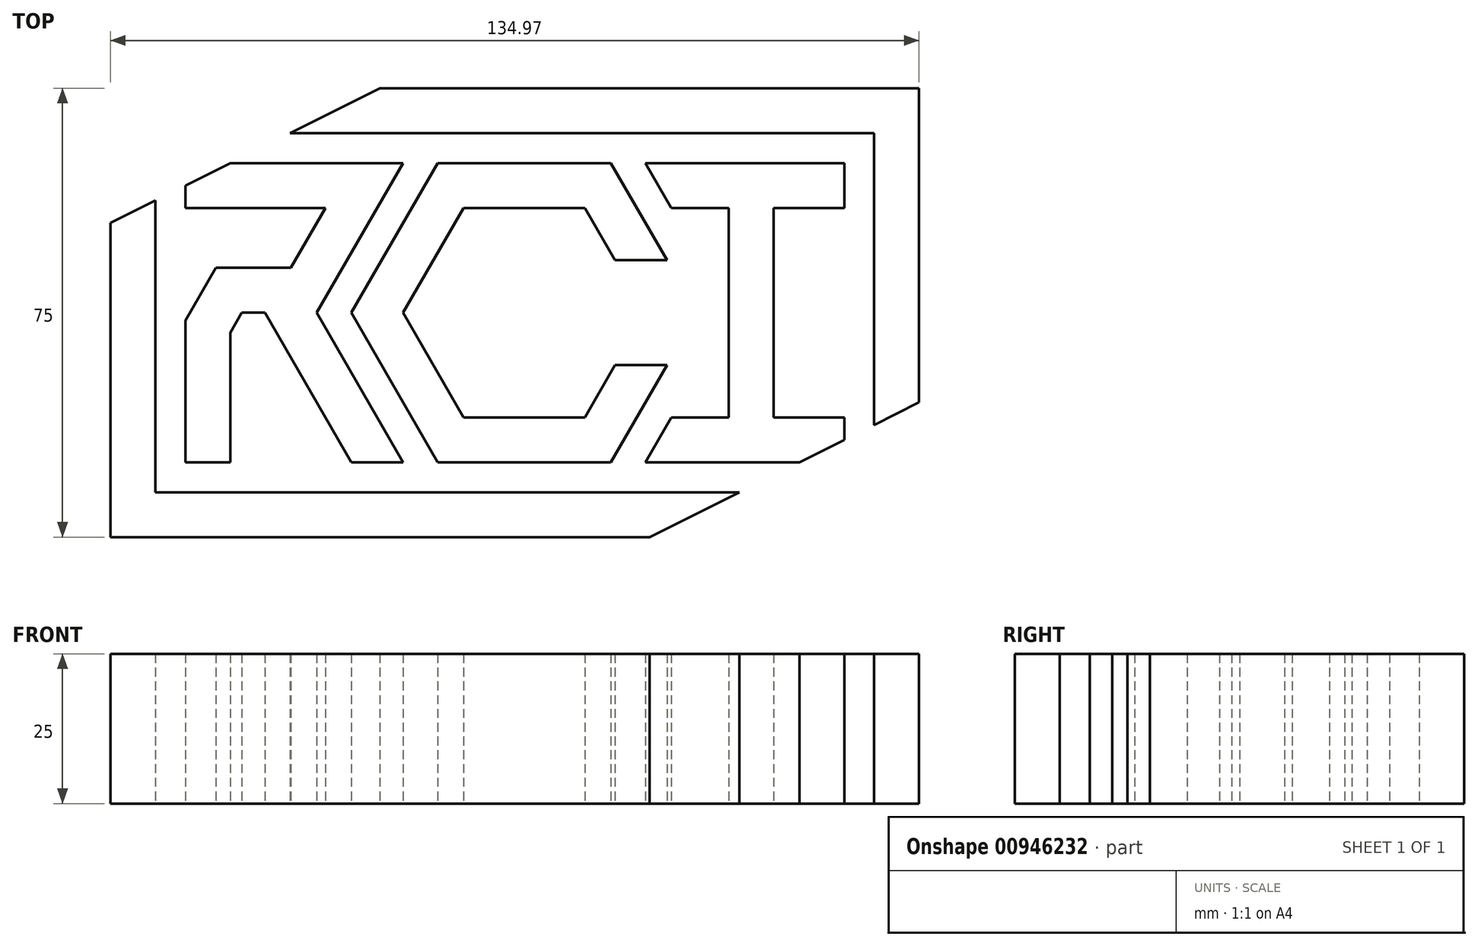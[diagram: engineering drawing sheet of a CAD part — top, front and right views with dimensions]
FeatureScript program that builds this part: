
annotation { "Feature Type Name" : "Feature", "Feature Type Description" : "" }
export const myFeature = defineFeature(function(context is Context, id is Id, definition is map)
    precondition{}
    {
        {
            var Q0;
            Q0=qCreatedBy(makeId("Top.planeOp"),FACE);
            var sketch = newSketch(context, id + "F0", { "sketchPlane" : qUnion([Q0])});
            skCircle(sketch, "E0.cCircle", {"center": v(0, 0) * mm, "radius": 17.5 * mm, "construction": true});
            skLineSegment(sketch, "E0.0", {"start": v(-10.1, 17.5) * mm, "end": v(10.1, 17.5) * mm});
            skLineSegment(sketch, "E0.1", {"start": v(10.1, 17.5) * mm, "end": v(15.16, 8.75) * mm});
            skLineSegment(sketch, "E0.2", {"start": v(15.16, -8.75) * mm, "end": v(10.1, -17.5) * mm});
            skLineSegment(sketch, "E0.3", {"start": v(10.1, -17.5) * mm, "end": v(-10.1, -17.5) * mm});
            skLineSegment(sketch, "E0.4", {"start": v(-10.1, -17.5) * mm, "end": v(-20.2, 0) * mm});
            skLineSegment(sketch, "E0.5", {"start": v(-20.2, 0) * mm, "end": v(-10.1, 17.5) * mm});
            skPoint(sketch, "E0.0.midPoint", {"position": v(0, 17.5) * mm});
            skLineSegment(sketch, "E1.0", {"start": v(-14.43, 25) * mm, "end": v(14.43, 25) * mm});
            skLineSegment(sketch, "E1.1", {"start": v(23.82, -8.75) * mm, "end": v(14.43, -25) * mm});
            skLineSegment(sketch, "E1.2", {"start": v(14.43, -25) * mm, "end": v(-14.43, -25) * mm});
            skLineSegment(sketch, "E1.3", {"start": v(14.43, 25) * mm, "end": v(23.82, 8.75) * mm});
            skLineSegment(sketch, "E1.4", {"start": v(-14.43, -25) * mm, "end": v(-28.87, 0) * mm});
            skLineSegment(sketch, "E1.5", {"start": v(-28.87, 0) * mm, "end": v(-14.43, 25) * mm});
            skPoint(sketch, "E2", {"position": v(15.16, -8.75) * mm});
            skPoint(sketch, "E3", {"position": v(15.16, 8.75) * mm});
            skLineSegment(sketch, "E4", {"start": v(15.16, 8.75) * mm, "end": v(23.82, 8.75) * mm});
            skLineSegment(sketch, "E5", {"start": v(15.16, -8.75) * mm, "end": v(23.82, -8.75) * mm});
            skPoint(sketch, "E6.orphan", {"position": v(20.2, 0) * mm});
            skLineSegment(sketch, "E7", {"start": v(85.6, -25) * mm, "end": v(-85.44, -25) * mm, "construction": true});
            skLineSegment(sketch, "E8", {"start": v(-85.44, -25) * mm, "end": v(-85.44, 25) * mm, "construction": true});
            skLineSegment(sketch, "E9", {"start": v(85.6, 25) * mm, "end": v(85.6, -25) * mm, "construction": true});
            skLineSegment(sketch, "E10", {"start": v(-85.44, 25) * mm, "end": v(0, 25) * mm, "construction": true});
            skPoint(sketch, "E11", {"position": v(0, 25) * mm});
            skLineSegment(sketch, "E12.0", {"start": v(-34.64, 0) * mm, "end": v(-23.24, 19.75) * mm});
            skLineSegment(sketch, "E12.1", {"start": v(-20.2, -25) * mm, "end": v(-34.64, 0) * mm});
            skLineSegment(sketch, "E13.0", {"start": v(-38.97, 7.5) * mm, "end": v(-33.2, 17.5) * mm});
            skLineSegment(sketch, "E13.1", {"start": v(-28.87, -25) * mm, "end": v(-43.3, 0) * mm});
            skLineSegment(sketch, "E14", {"start": v(-20.2, 25) * mm, "end": v(-49.07, 25) * mm});
            skLineSegment(sketch, "E15.0", {"start": v(-33.2, 17.5) * mm, "end": v(-49.07, 17.5) * mm});
            skLineSegment(sketch, "E16", {"start": v(-43.3, 0) * mm, "end": v(-47.15, 0) * mm});
            skLineSegment(sketch, "E17.0", {"start": v(-38.97, 7.5) * mm, "end": v(-49.07, 7.5) * mm});
            skLineSegment(sketch, "E18", {"start": v(-20.2, -25) * mm, "end": v(-28.87, -25) * mm});
            skLineSegment(sketch, "E19", {"start": v(-49.07, -3.33) * mm, "end": v(-49.07, -25) * mm});
            skLineSegment(sketch, "E20.0", {"start": v(-56.57, -1.32) * mm, "end": v(-56.57, -25) * mm});
            skLineSegment(sketch, "E21", {"start": v(-56.57, -25) * mm, "end": v(-49.07, -25) * mm});
            skLineSegment(sketch, "E22", {"start": v(-49.07, 7.5) * mm, "end": v(-51.48, 7.5) * mm});
            skLineSegment(sketch, "E23", {"start": v(-51.48, 7.5) * mm, "end": v(-56.57, -1.32) * mm});
            skLineSegment(sketch, "E24", {"start": v(-49.07, 25) * mm, "end": v(-56.57, 21.25) * mm});
            skLineSegment(sketch, "E25", {"start": v(-56.57, 21.25) * mm, "end": v(-56.57, 17.5) * mm});
            skLineSegment(sketch, "E26", {"start": v(-49.07, 17.5) * mm, "end": v(-56.57, 17.5) * mm});
            skLineSegment(sketch, "E27", {"start": v(-23.24, 19.75) * mm, "end": v(-20.2, 25) * mm});
            skLineSegment(sketch, "E28", {"start": v(-77.06, 17.5) * mm, "end": v(-77.06, 25) * mm, "construction": true});
            skPoint(sketch, "E29", {"position": v(-77.06, 21.25) * mm});
            skLineSegment(sketch, "E30", {"start": v(-77.06, 17.5) * mm, "end": v(-85.44, 17.5) * mm, "construction": true});
            skLineSegment(sketch, "E31", {"start": v(-56.57, -25) * mm, "end": v(-85.44, -25) * mm, "construction": true});
            skLineSegment(sketch, "E32", {"start": v(0, 25) * mm, "end": v(85.6, 25) * mm, "construction": true});
            skLineSegment(sketch, "E33.0", {"start": v(-47.15, 0) * mm, "end": v(-49.07, -3.33) * mm});
            skPoint(sketch, "E34.orphan", {"position": v(-49.07, 0) * mm});
            skLineSegment(sketch, "E35", {"start": v(20.2, 25) * mm, "end": v(53.4, 25) * mm});
            skLineSegment(sketch, "E36", {"start": v(53.4, 25) * mm, "end": v(53.4, 17.5) * mm});
            skLineSegment(sketch, "E37", {"start": v(53.4, 17.5) * mm, "end": v(24.54, 17.5) * mm});
            skLineSegment(sketch, "E38", {"start": v(24.54, 17.5) * mm, "end": v(20.2, 25) * mm});
            skLineSegment(sketch, "E39", {"start": v(0, 0) * mm, "end": v(85.6, 0) * mm, "construction": true});
            skLineSegment(sketch, "E40.MirrorCS", {"start": v(53.4, -17.5) * mm, "end": v(41.64, -17.5) * mm});
            skLineSegment(sketch, "E41.MirrorCS", {"start": v(24.54, -17.5) * mm, "end": v(20.2, -25) * mm});
            skLineSegment(sketch, "E42.MirrorCS", {"start": v(20.2, -25) * mm, "end": v(53.4, -25) * mm});
            skLineSegment(sketch, "E43.MirrorCS", {"start": v(53.4, -21.25) * mm, "end": v(53.4, -17.5) * mm});
            skLineSegment(sketch, "E44", {"start": v(53.4, -21.25) * mm, "end": v(45.9, -25) * mm});
            skPoint(sketch, "E45.orphan", {"position": v(53.4, -25) * mm});
            skPoint(sketch, "E46", {"position": v(38.97, 17.5) * mm});
            skPoint(sketch, "E47", {"position": v(36.8, 25) * mm});
            skLineSegment(sketch, "E48", {"start": v(38.97, 13.44) * mm, "end": v(36.8, 13.44) * mm, "construction": true});
            skPoint(sketch, "E49", {"position": v(37.89, 13.44) * mm});
            skLineSegment(sketch, "E50", {"start": v(37.89, 17.5) * mm, "end": v(37.89, -17.5) * mm, "construction": true});
            skLineSegment(sketch, "E51.0", {"start": v(34.14, 17.5) * mm, "end": v(34.14, -17.5) * mm});
            skLineSegment(sketch, "E52", {"start": v(41.64, -17.5) * mm, "end": v(41.64, 17.5) * mm});
            skLineSegment(sketch, "E53", {"start": v(34.14, -17.5) * mm, "end": v(24.54, -17.5) * mm});
            skLineSegment(sketch, "E54", {"start": v(41.64, -17.5) * mm, "end": v(34.14, -17.5) * mm, "construction": true});
            skSolve(sketch);
        }
        {
            var Q0;
            Q0=qCreatedBy(makeId("Top.planeOp"),FACE);
            var sketch = newSketch(context, id + "F1", { "sketchPlane" : qUnion([Q0])});
            skLineSegment(sketch, "E55", {"start": v(-61.57, 18.75) * mm, "end": v(-61.57, -30) * mm});
            skLineSegment(sketch, "E56", {"start": v(-61.57, -30) * mm, "end": v(35.9, -30) * mm});
            skLineSegment(sketch, "E57", {"start": v(-61.57, 18.75) * mm, "end": v(-69.07, 15) * mm});
            skLineSegment(sketch, "E58", {"start": v(-69.07, 15) * mm, "end": v(-69.07, -37.5) * mm});
            skLineSegment(sketch, "E59", {"start": v(-69.07, -37.5) * mm, "end": v(20.9, -37.5) * mm});
            skLineSegment(sketch, "E60", {"start": v(20.9, -37.5) * mm, "end": v(35.9, -30) * mm});
            skLineSegment(sketch, "E61", {"start": v(-39.07, 30) * mm, "end": v(-61.57, 18.75) * mm, "construction": true});
            skLineSegment(sketch, "E62", {"start": v(58.4, -18.75) * mm, "end": v(35.9, -30) * mm, "construction": true});
            skLineSegment(sketch, "E63", {"start": v(-39.07, 30) * mm, "end": v(58.4, 30) * mm});
            skLineSegment(sketch, "E64", {"start": v(58.4, 30) * mm, "end": v(58.4, -18.75) * mm});
            skLineSegment(sketch, "E65.0", {"start": v(65.9, 37.5) * mm, "end": v(65.9, -15) * mm});
            skLineSegment(sketch, "E65.1", {"start": v(-24.07, 37.5) * mm, "end": v(65.9, 37.5) * mm});
            skLineSegment(sketch, "E66", {"start": v(58.4, -18.75) * mm, "end": v(65.9, -15) * mm});
            skLineSegment(sketch, "E67", {"start": v(-39.07, 30) * mm, "end": v(-24.07, 37.5) * mm});
            skSolve(sketch);
        }
        {
            var Q0;
            Q0=qCreatedBy(makeId("Top.planeOp"),FACE);
            var sketch = newSketch(context, id + "F2", { "sketchPlane" : qUnion([Q0])});
            skLineSegment(sketch, "E68.0.0", {"start": v(-69.07, -37.5) * mm, "end": v(20.9, -37.5) * mm});
            skLineSegment(sketch, "E68.0.1", {"start": v(20.9, -37.5) * mm, "end": v(35.9, -30) * mm});
            skLineSegment(sketch, "E68.0.2", {"start": v(35.9, -30) * mm, "end": v(-61.57, -30) * mm});
            skLineSegment(sketch, "E68.0.3", {"start": v(-61.57, -30) * mm, "end": v(-61.57, 18.75) * mm});
            skLineSegment(sketch, "E68.0.4", {"start": v(-61.57, 18.75) * mm, "end": v(-69.07, 15) * mm});
            skLineSegment(sketch, "E68.0.5", {"start": v(-69.07, 15) * mm, "end": v(-69.07, -37.5) * mm});
            skLineSegment(sketch, "E69.0.0", {"start": v(-49.07, 7.5) * mm, "end": v(-51.48, 7.5) * mm});
            skLineSegment(sketch, "E69.0.1", {"start": v(-51.48, 7.5) * mm, "end": v(-56.57, -1.32) * mm});
            skLineSegment(sketch, "E69.0.2", {"start": v(-56.57, -1.32) * mm, "end": v(-56.57, -25) * mm});
            skLineSegment(sketch, "E69.0.3", {"start": v(-56.57, -25) * mm, "end": v(-49.07, -25) * mm});
            skLineSegment(sketch, "E69.0.4", {"start": v(-49.07, -25) * mm, "end": v(-49.07, -3.33) * mm});
            skLineSegment(sketch, "E69.0.5", {"start": v(-49.07, -3.33) * mm, "end": v(-47.15, 0) * mm});
            skLineSegment(sketch, "E69.0.6", {"start": v(-47.15, 0) * mm, "end": v(-43.3, 0) * mm});
            skLineSegment(sketch, "E69.0.7", {"start": v(-43.3, 0) * mm, "end": v(-28.87, -25) * mm});
            skLineSegment(sketch, "E69.0.8", {"start": v(-28.87, -25) * mm, "end": v(-20.2, -25) * mm});
            skLineSegment(sketch, "E69.0.9", {"start": v(-20.2, -25) * mm, "end": v(-34.64, 0) * mm});
            skLineSegment(sketch, "E69.0.10", {"start": v(-34.64, 0) * mm, "end": v(-23.24, 19.75) * mm});
            skLineSegment(sketch, "E69.0.11", {"start": v(-23.24, 19.75) * mm, "end": v(-20.2, 25) * mm});
            skLineSegment(sketch, "E69.0.12", {"start": v(-20.2, 25) * mm, "end": v(-49.07, 25) * mm});
            skLineSegment(sketch, "E69.0.13", {"start": v(-49.07, 25) * mm, "end": v(-56.57, 21.25) * mm});
            skLineSegment(sketch, "E69.0.14", {"start": v(-56.57, 21.25) * mm, "end": v(-56.57, 17.5) * mm});
            skLineSegment(sketch, "E69.0.15", {"start": v(-56.57, 17.5) * mm, "end": v(-49.07, 17.5) * mm});
            skLineSegment(sketch, "E69.0.16", {"start": v(-49.07, 17.5) * mm, "end": v(-33.2, 17.5) * mm});
            skLineSegment(sketch, "E69.0.17", {"start": v(-33.2, 17.5) * mm, "end": v(-38.97, 7.5) * mm});
            skLineSegment(sketch, "E69.0.18", {"start": v(-38.97, 7.5) * mm, "end": v(-49.07, 7.5) * mm});
            skLineSegment(sketch, "E70.0.0", {"start": v(65.9, 37.5) * mm, "end": v(-24.07, 37.5) * mm});
            skLineSegment(sketch, "E70.0.1", {"start": v(-24.07, 37.5) * mm, "end": v(-39.07, 30) * mm});
            skLineSegment(sketch, "E70.0.2", {"start": v(-39.07, 30) * mm, "end": v(58.4, 30) * mm});
            skLineSegment(sketch, "E70.0.3", {"start": v(58.4, 30) * mm, "end": v(58.4, -18.75) * mm});
            skLineSegment(sketch, "E70.0.4", {"start": v(58.4, -18.75) * mm, "end": v(65.9, -15) * mm});
            skLineSegment(sketch, "E70.0.5", {"start": v(65.9, -15) * mm, "end": v(65.9, 37.5) * mm});
            skLineSegment(sketch, "E71.0.0", {"start": v(-14.43, -25) * mm, "end": v(14.43, -25) * mm});
            skLineSegment(sketch, "E71.0.1", {"start": v(14.43, -25) * mm, "end": v(23.82, -8.75) * mm});
            skLineSegment(sketch, "E71.0.2", {"start": v(23.82, -8.75) * mm, "end": v(15.16, -8.75) * mm});
            skLineSegment(sketch, "E71.0.3", {"start": v(15.16, -8.75) * mm, "end": v(10.1, -17.5) * mm});
            skLineSegment(sketch, "E71.0.4", {"start": v(10.1, -17.5) * mm, "end": v(-10.1, -17.5) * mm});
            skLineSegment(sketch, "E71.0.5", {"start": v(-10.1, -17.5) * mm, "end": v(-20.2, 0) * mm});
            skLineSegment(sketch, "E71.0.6", {"start": v(-20.2, 0) * mm, "end": v(-10.1, 17.5) * mm});
            skLineSegment(sketch, "E71.0.7", {"start": v(-10.1, 17.5) * mm, "end": v(10.1, 17.5) * mm});
            skLineSegment(sketch, "E71.0.8", {"start": v(10.1, 17.5) * mm, "end": v(15.16, 8.75) * mm});
            skLineSegment(sketch, "E71.0.9", {"start": v(15.16, 8.75) * mm, "end": v(23.82, 8.75) * mm});
            skLineSegment(sketch, "E71.0.10", {"start": v(23.82, 8.75) * mm, "end": v(14.43, 25) * mm});
            skLineSegment(sketch, "E71.0.11", {"start": v(14.43, 25) * mm, "end": v(-14.43, 25) * mm});
            skLineSegment(sketch, "E71.0.12", {"start": v(-14.43, 25) * mm, "end": v(-28.87, 0) * mm});
            skLineSegment(sketch, "E71.0.13", {"start": v(-28.87, 0) * mm, "end": v(-14.43, -25) * mm});
            skLineSegment(sketch, "E72.0.0", {"start": v(41.64, 17.5) * mm, "end": v(34.14, 17.5) * mm});
            skLineSegment(sketch, "E72.0.1", {"start": v(34.14, 17.5) * mm, "end": v(34.14, -17.5) * mm});
            skLineSegment(sketch, "E72.0.2", {"start": v(34.14, -17.5) * mm, "end": v(24.54, -17.5) * mm});
            skLineSegment(sketch, "E72.0.3", {"start": v(24.54, -17.5) * mm, "end": v(20.2, -25) * mm});
            skLineSegment(sketch, "E72.0.4", {"start": v(20.2, -25) * mm, "end": v(45.9, -25) * mm});
            skLineSegment(sketch, "E72.0.5", {"start": v(45.9, -25) * mm, "end": v(53.4, -21.25) * mm});
            skLineSegment(sketch, "E72.0.6", {"start": v(53.4, -21.25) * mm, "end": v(53.4, -17.5) * mm});
            skLineSegment(sketch, "E72.0.7", {"start": v(53.4, -17.5) * mm, "end": v(41.64, -17.5) * mm});
            skLineSegment(sketch, "E72.0.8", {"start": v(41.64, -17.5) * mm, "end": v(41.64, 17.5) * mm});
            skLineSegment(sketch, "E73.0.0", {"start": v(34.14, 17.5) * mm, "end": v(41.64, 17.5) * mm});
            skLineSegment(sketch, "E73.0.1", {"start": v(41.64, 17.5) * mm, "end": v(53.4, 17.5) * mm});
            skLineSegment(sketch, "E73.0.2", {"start": v(53.4, 17.5) * mm, "end": v(53.4, 25) * mm});
            skLineSegment(sketch, "E73.0.3", {"start": v(53.4, 25) * mm, "end": v(20.2, 25) * mm});
            skLineSegment(sketch, "E73.0.4", {"start": v(20.2, 25) * mm, "end": v(24.54, 17.5) * mm});
            skLineSegment(sketch, "E73.0.5", {"start": v(24.54, 17.5) * mm, "end": v(34.14, 17.5) * mm});
            skSolve(sketch);
        }
        {
            var Q0;
            Q0 = qSketchRegion(id + "F2", true);
            extrude(context, id + "F3", {"entities" : qUnion([Q0]), "depth" : 25 * mm, "offsetDistance" : 25 * mm});
        }
    });
